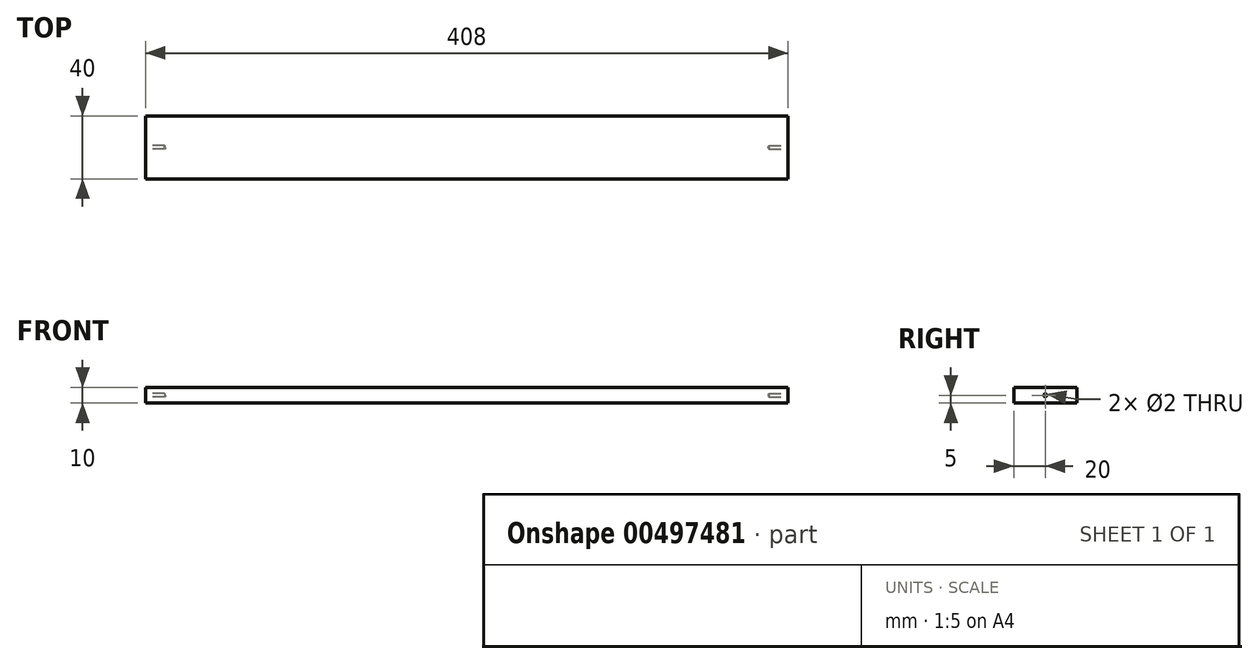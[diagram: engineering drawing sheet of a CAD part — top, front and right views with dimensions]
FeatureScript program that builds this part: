
annotation { "Feature Type Name" : "Feature", "Feature Type Description" : "" }
export const myFeature = defineFeature(function(context is Context, id is Id, definition is map)
    precondition{}
    {
        {
            var Q0;
            Q0=qCreatedBy(makeId("Top.planeOp"),FACE);
            var sketch = newSketch(context, id + "F0", { "sketchPlane" : qUnion([Q0])});
            skLineSegment(sketch, "E0.bottom", {"start": v(0, 0) * mm, "end": v(-204, 0) * mm});
            skLineSegment(sketch, "E0.top", {"start": v(0, -20) * mm, "end": v(-204, -20) * mm});
            skLineSegment(sketch, "E0.left", {"start": v(0, 0) * mm, "end": v(0, -20) * mm});
            skLineSegment(sketch, "E0.right", {"start": v(-204, 0) * mm, "end": v(-204, -20) * mm});
            skSolve(sketch);
        }
        {
            var Q0;
            Q0=qSketchRegion(id+"F0",true);
            extrude(context, id + "F1", {"entities" : qUnion([Q0]), "depth" : 10 * mm});
        }
        {
            var Q0;
            Q0=makeQuery(id+"F1.opExtrude","SWEPT_FACE",FACE,{"disambiguationData":[OSD([sQuery(id+"F0.wireOp",EDGE,"E0.right")])]});
            var sketch = newSketch(context, id + "F2", { "sketchPlane" : qUnion([Q0])});
            skPoint(sketch, "E1", {"position": v(20, 5) * mm});
            skPoint(sketch, "E2", {"position": v(0, 5) * mm});
            skSolve(sketch);
        }
        {
            var Q0;
            Q0=sQuery(id+"F2.wireOp",VERTEX,"E2");
            var Q1;
            Q1=makeQuery(id+"F1.opExtrude","SWEPT_BODY",BODY,{"disambiguationData":[OSD([sQuery(id+"F0.wireOp",EDGE,"E0.bottom"),sQuery(id+"F0.wireOp",EDGE,"E0.top"),sQuery(id+"F0.wireOp",EDGE,"E0.left"),sQuery(id+"F0.wireOp",EDGE,"E0.right")])]});
            hole(context, id + "F3", {"style" : HoleStyle.SIMPLE, "endStyle" : HoleEndStyle.BLIND, "holeDiameter" : 2 * mm, "holeDepth" : 12 * mm, "isTappedThrough" : true, "tappedDepth" : 12 * mm, "tapClearance" : 3, "locations" : qUnion([Q0]), "scope" : qUnion([Q1])});
        }
        {
            var Q0;
            Q0=makeQuery(id+"F1.opExtrude","SWEPT_BODY",BODY,{"disambiguationData":[OSD([sQuery(id+"F0.wireOp",EDGE,"E0.bottom"),sQuery(id+"F0.wireOp",EDGE,"E0.top"),sQuery(id+"F0.wireOp",EDGE,"E0.left"),sQuery(id+"F0.wireOp",EDGE,"E0.right")])]});
            var Q1;
            Q1=qCreatedBy(makeId("Front.planeOp"),FACE);
            mirror(context, id + "F4", {"operationType" : NewBodyOperationType.ADD, "entities" : qUnion([Q0]), "mirrorPlane" : qUnion([Q1])});
        }
        {
            var Q0;
            Q0=makeQuery(id+"F1.opExtrude","SWEPT_BODY",BODY,{"disambiguationData":[OSD([sQuery(id+"F0.wireOp",EDGE,"E0.bottom"),sQuery(id+"F0.wireOp",EDGE,"E0.top"),sQuery(id+"F0.wireOp",EDGE,"E0.left"),sQuery(id+"F0.wireOp",EDGE,"E0.right")])]});
            var Q1;
            Q1=qCreatedBy(makeId("Right.planeOp"),FACE);
            mirror(context, id + "F5", {"operationType" : NewBodyOperationType.ADD, "entities" : qUnion([Q0]), "mirrorPlane" : qUnion([Q1])});
        }
    });
